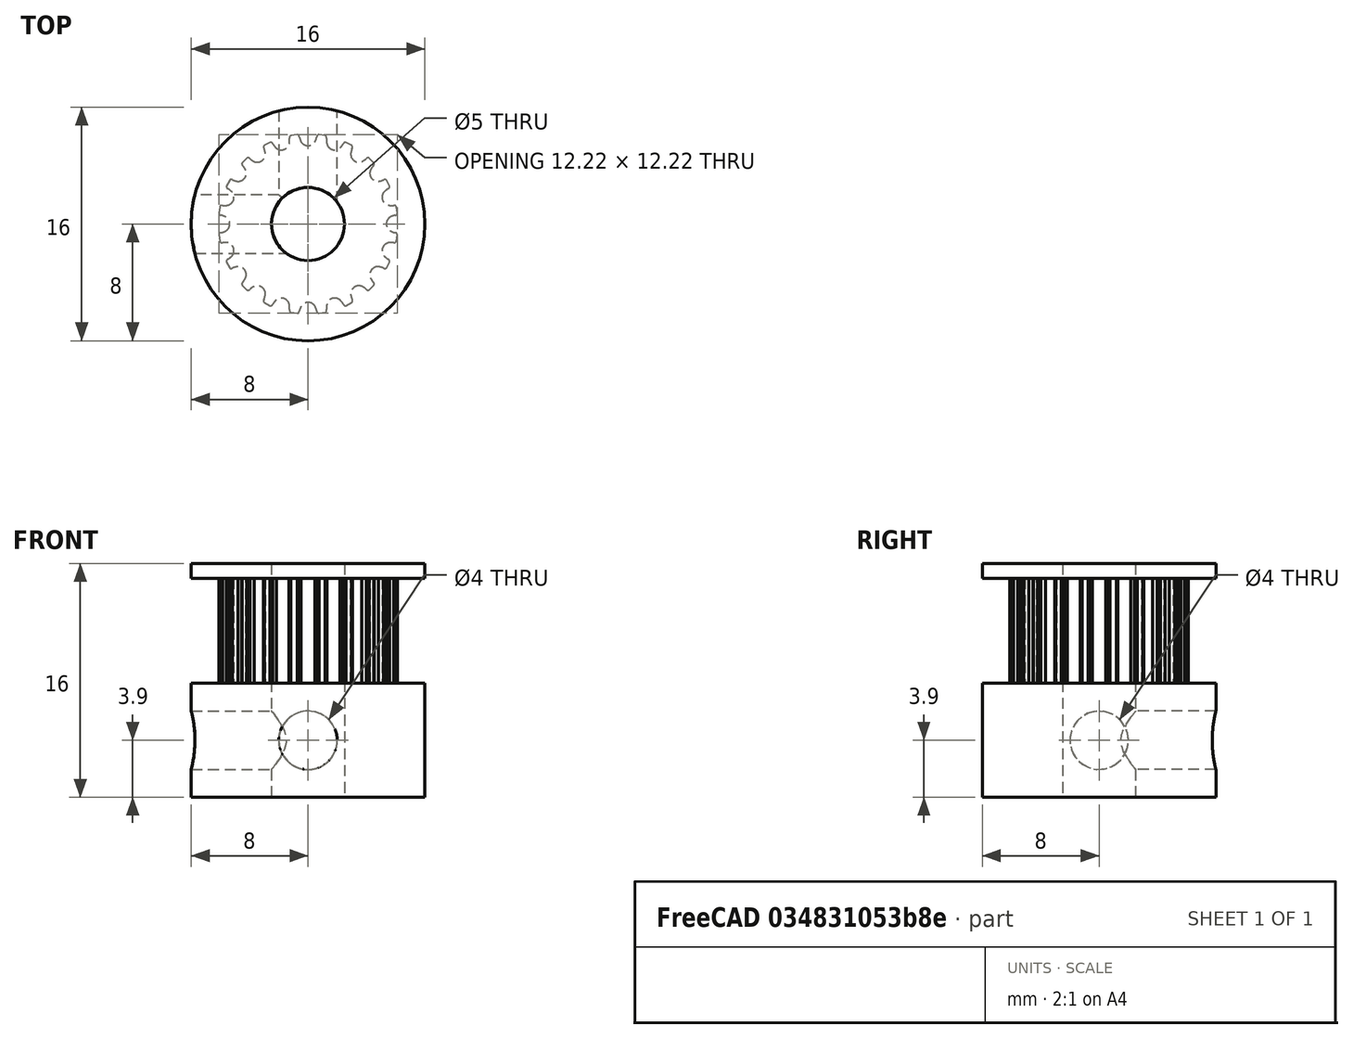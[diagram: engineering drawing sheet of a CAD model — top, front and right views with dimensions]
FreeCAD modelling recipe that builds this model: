
FCSTD DOCUMENT  (FreeCAD 0.21R33771 (Git))
Label: timing_pulley_gt2_20teeth_bore5
License: All rights reserved
LicenseURL: http://en.wikipedia.org/wiki/All_rights_reserved
objects: Sketcher::SketchObject×5, PartDesign::Pad×3, PartDesign::Pocket×2, PartDesign::Body×1
note: 16 computed .brp shape members not serialized (recipe doc carries the construction recipe); baked Part::Feature solids carry a one-line shape summary decoded from their .brp

FEATURE [Sketcher::SketchObject] SketchGear
  FullyConstrained = false
  MapMode = 5
  Support = -> [XY_Plane]
  sketch-geometry (121):
    g0: ArcOfCircle CenterX=5.9622 CenterY=-0.75 CenterZ=0 NormalX=0 NormalY=0 NormalZ=1 AngleXU=8.1e-15 Radius=0.15 StartAngle=0 EndAngle=1.5708
    g1: ArcOfCircle CenterX=6.30816 CenterY=0.82798 CenterZ=0 NormalX=0 NormalY=0 NormalZ=-1 AngleXU=-1.3331 Radius=1.46929 StartAngle=0 EndAngle=0.255762
    g2: ArcOfCircle CenterX=5.92156 CenterY=0 CenterZ=0 NormalX=0 NormalY=0 NormalZ=-1 AngleXU=-0.984764 Radius=0.559359 StartAngle=0 EndAngle=1.96953
    g3: ArcOfCircle CenterX=6.30816 CenterY=-0.82798 CenterZ=0 NormalX=0 NormalY=0 NormalZ=-1 AngleXU=1.07734 Radius=1.46929 StartAngle=0 EndAngle=0.255762
    g4: ArcOfCircle CenterX=5.9622 CenterY=0.75 CenterZ=0 NormalX=0 NormalY=0 NormalZ=1 AngleXU=-1.5708 Radius=0.15 StartAngle=0 EndAngle=1.5708
    g5: LineSegment StartX=6.1122 StartY=0.75 StartZ=0 EndX=6.04481 EndY=1.17548 EndZ=0
    g6: ArcOfCircle CenterX=5.90215 CenterY=1.12913 CenterZ=0 NormalX=0 NormalY=0 NormalZ=1 AngleXU=0.314159 Radius=0.15 StartAngle=0 EndAngle=1.5708
    g7: ArcOfCircle CenterX=5.74356 CenterY=2.73679 CenterZ=0 NormalX=0 NormalY=0 NormalZ=-1 AngleXU=-1.64726 Radius=1.46929 StartAngle=0 EndAngle=0.255762
    g8: ArcOfCircle CenterX=5.63174 CenterY=1.82986 CenterZ=0 NormalX=0 NormalY=0 NormalZ=-1 AngleXU=-1.29892 Radius=0.559359 StartAngle=0 EndAngle=1.96953
    g9: ArcOfCircle CenterX=6.25528 CenterY=1.16187 CenterZ=0 NormalX=0 NormalY=0 NormalZ=-1 AngleXU=0.763178 Radius=1.46929 StartAngle=0 EndAngle=0.255762
    g10: ArcOfCircle CenterX=5.43862 CenterY=2.55571 CenterZ=0 NormalX=0 NormalY=0 NormalZ=1 AngleXU=-1.25664 Radius=0.15 StartAngle=0 EndAngle=1.5708
    g11: LineSegment StartX=5.58128 StartY=2.60207 StartZ=0 EndX=5.38571 EndY=2.9859 EndZ=0
    g12: ArcOfCircle CenterX=5.26436 CenterY=2.89773 CenterZ=0 NormalX=0 NormalY=0 NormalZ=1 AngleXU=0.628319 Radius=0.15 StartAngle=0 EndAngle=1.5708
    g13: ArcOfCircle CenterX=4.61674 CenterY=4.3777 CenterZ=0 NormalX=0 NormalY=0 NormalZ=-1 AngleXU=-1.96142 Radius=1.46929 StartAngle=0 EndAngle=0.255762
    g14: ArcOfCircle CenterX=4.79064 CenterY=3.4806 CenterZ=0 NormalX=0 NormalY=0 NormalZ=-1 AngleXU=-1.61308 Radius=0.559359 StartAngle=0 EndAngle=1.96953
    g15: ArcOfCircle CenterX=5.59009 CenterY=3.038 CenterZ=0 NormalX=0 NormalY=0 NormalZ=-1 AngleXU=0.449019 Radius=1.46929 StartAngle=0 EndAngle=0.255762
    g16: ArcOfCircle CenterX=4.38268 CenterY=4.11125 CenterZ=0 NormalX=0 NormalY=0 NormalZ=1 AngleXU=-0.942478 Radius=0.15 StartAngle=0 EndAngle=1.5708
    g17: LineSegment StartX=4.50403 StartY=4.19942 StartZ=0 EndX=4.19942 EndY=4.50403 EndZ=0
    g18: ArcOfCircle CenterX=4.11125 CenterY=4.38268 CenterZ=0 NormalX=0 NormalY=0 NormalZ=1 AngleXU=0.942478 Radius=0.15 StartAngle=0 EndAngle=1.5708
    g19: ArcOfCircle CenterX=3.038 CenterY=5.59009 CenterZ=0 NormalX=0 NormalY=0 NormalZ=-1 AngleXU=-2.27558 Radius=1.46929 StartAngle=0 EndAngle=0.255762
    g20: ArcOfCircle CenterX=3.4806 CenterY=4.79064 CenterZ=0 NormalX=0 NormalY=0 NormalZ=-1 AngleXU=-1.92724 Radius=0.559359 StartAngle=0 EndAngle=1.96953
    g21: ArcOfCircle CenterX=4.3777 CenterY=4.61674 CenterZ=0 NormalX=0 NormalY=0 NormalZ=-1 AngleXU=0.13486 Radius=1.46929 StartAngle=0 EndAngle=0.255762
    g22: ArcOfCircle CenterX=2.89773 CenterY=5.26436 CenterZ=0 NormalX=0 NormalY=0 NormalZ=1 AngleXU=-0.628319 Radius=0.15 StartAngle=0 EndAngle=1.5708
    g23: LineSegment StartX=2.9859 StartY=5.38571 StartZ=0 EndX=2.60207 EndY=5.58128 EndZ=0
    g24: ArcOfCircle CenterX=2.55571 CenterY=5.43862 CenterZ=0 NormalX=0 NormalY=0 NormalZ=1 AngleXU=1.25664 Radius=0.15 StartAngle=0 EndAngle=1.5708
    g25: ArcOfCircle CenterX=1.16187 CenterY=6.25528 CenterZ=0 NormalX=0 NormalY=0 NormalZ=-1 AngleXU=-2.58974 Radius=1.46929 StartAngle=0 EndAngle=0.255762
    g26: ArcOfCircle CenterX=1.82986 CenterY=5.63174 CenterZ=0 NormalX=0 NormalY=0 NormalZ=-1 AngleXU=-2.2414 Radius=0.559359 StartAngle=0 EndAngle=1.96953
    g27: ArcOfCircle CenterX=2.73679 CenterY=5.74356 CenterZ=0 NormalX=0 NormalY=0 NormalZ=-1 AngleXU=-0.1793 Radius=1.46929 StartAngle=0 EndAngle=0.255762
    g28: ArcOfCircle CenterX=1.12913 CenterY=5.90215 CenterZ=0 NormalX=0 NormalY=0 NormalZ=1 AngleXU=-0.314159 Radius=0.15 StartAngle=0 EndAngle=1.5708
    g29: LineSegment StartX=1.17548 StartY=6.04481 StartZ=0 EndX=0.75 EndY=6.1122 EndZ=0
    g30: ArcOfCircle CenterX=0.75 CenterY=5.9622 CenterZ=0 NormalX=0 NormalY=0 NormalZ=1 AngleXU=1.5708 Radius=0.15 StartAngle=0 EndAngle=1.5708
    g31: ArcOfCircle CenterX=-0.82798 CenterY=6.30816 CenterZ=0 NormalX=0 NormalY=0 NormalZ=-1 AngleXU=-2.9039 Radius=1.46929 StartAngle=0 EndAngle=0.255762
    g32: ArcOfCircle CenterX=3e-16 CenterY=5.92156 CenterZ=0 NormalX=0 NormalY=0 NormalZ=-1 AngleXU=-2.55556 Radius=0.559359 StartAngle=0 EndAngle=1.96953
    g33: ArcOfCircle CenterX=0.82798 CenterY=6.30816 CenterZ=0 NormalX=0 NormalY=0 NormalZ=-1 AngleXU=-0.493459 Radius=1.46929 StartAngle=0 EndAngle=0.255762
    g34: ArcOfCircle CenterX=-0.75 CenterY=5.9622 CenterZ=0 NormalX=0 NormalY=0 NormalZ=1 AngleXU=5.9e-15 Radius=0.15 StartAngle=0 EndAngle=1.5708
    g35: LineSegment StartX=-0.75 StartY=6.1122 StartZ=0 EndX=-1.17548 EndY=6.04481 EndZ=0
    g36: ArcOfCircle CenterX=-1.12913 CenterY=5.90215 CenterZ=0 NormalX=0 NormalY=0 NormalZ=1 AngleXU=1.88496 Radius=0.15 StartAngle=0 EndAngle=1.5708
    g37: ArcOfCircle CenterX=-2.73679 CenterY=5.74356 CenterZ=0 NormalX=0 NormalY=0 NormalZ=-1 AngleXU=3.06513 Radius=1.46929 StartAngle=0 EndAngle=0.255762
    g38: ArcOfCircle CenterX=-1.82986 CenterY=5.63174 CenterZ=0 NormalX=0 NormalY=0 NormalZ=-1 AngleXU=-2.86972 Radius=0.559359 StartAngle=0 EndAngle=1.96953
    g39: ArcOfCircle CenterX=-1.16187 CenterY=6.25528 CenterZ=0 NormalX=0 NormalY=0 NormalZ=-1 AngleXU=-0.807618 Radius=1.46929 StartAngle=0 EndAngle=0.255762
    g40: ArcOfCircle CenterX=-2.55571 CenterY=5.43862 CenterZ=0 NormalX=0 NormalY=0 NormalZ=1 AngleXU=0.314159 Radius=0.15 StartAngle=0 EndAngle=1.5708
    g41: LineSegment StartX=-2.60207 StartY=5.58128 StartZ=0 EndX=-2.9859 EndY=5.38571 EndZ=0
    g42: ArcOfCircle CenterX=-2.89773 CenterY=5.26436 CenterZ=0 NormalX=0 NormalY=0 NormalZ=1 AngleXU=2.19911 Radius=0.15 StartAngle=0 EndAngle=1.5708
    g43: ArcOfCircle CenterX=-4.3777 CenterY=4.61674 CenterZ=0 NormalX=0 NormalY=0 NormalZ=-1 AngleXU=2.75097 Radius=1.46929 StartAngle=0 EndAngle=0.255762
    g44: ArcOfCircle CenterX=-3.4806 CenterY=4.79064 CenterZ=0 NormalX=0 NormalY=0 NormalZ=-1 AngleXU=3.09931 Radius=0.559359 StartAngle=0 EndAngle=1.96953
    g45: ArcOfCircle CenterX=-3.038 CenterY=5.59009 CenterZ=0 NormalX=0 NormalY=0 NormalZ=-1 AngleXU=-1.12178 Radius=1.46929 StartAngle=0 EndAngle=0.255762
    g46: ArcOfCircle CenterX=-4.11125 CenterY=4.38268 CenterZ=0 NormalX=0 NormalY=0 NormalZ=1 AngleXU=0.628319 Radius=0.15 StartAngle=0 EndAngle=1.5708
    g47: LineSegment StartX=-4.19942 StartY=4.50403 StartZ=0 EndX=-4.50403 EndY=4.19942 EndZ=0
    g48: ArcOfCircle CenterX=-4.38268 CenterY=4.11125 CenterZ=0 NormalX=0 NormalY=0 NormalZ=1 AngleXU=2.51327 Radius=0.15 StartAngle=0 EndAngle=1.5708
    g49: ArcOfCircle CenterX=-5.59009 CenterY=3.038 CenterZ=0 NormalX=0 NormalY=0 NormalZ=-1 AngleXU=2.43681 Radius=1.46929 StartAngle=0 EndAngle=0.255762
    g50: ArcOfCircle CenterX=-4.79064 CenterY=3.4806 CenterZ=0 NormalX=0 NormalY=0 NormalZ=-1 AngleXU=2.78515 Radius=0.559359 StartAngle=0 EndAngle=1.96953
    g51: ArcOfCircle CenterX=-4.61674 CenterY=4.3777 CenterZ=0 NormalX=0 NormalY=0 NormalZ=-1 AngleXU=-1.43594 Radius=1.46929 StartAngle=0 EndAngle=0.255762
    g52: ArcOfCircle CenterX=-5.26436 CenterY=2.89773 CenterZ=0 NormalX=0 NormalY=0 NormalZ=1 AngleXU=0.942478 Radius=0.15 StartAngle=0 EndAngle=1.5708
    g53: LineSegment StartX=-5.38571 StartY=2.9859 StartZ=0 EndX=-5.58128 EndY=2.60207 EndZ=0
    g54: ArcOfCircle CenterX=-5.43862 CenterY=2.55571 CenterZ=0 NormalX=0 NormalY=0 NormalZ=1 AngleXU=2.82743 Radius=0.15 StartAngle=0 EndAngle=1.5708
    g55: ArcOfCircle CenterX=-6.25528 CenterY=1.16187 CenterZ=0 NormalX=0 NormalY=0 NormalZ=-1 AngleXU=2.12265 Radius=1.46929 StartAngle=0 EndAngle=0.255762
    g56: ArcOfCircle CenterX=-5.63174 CenterY=1.82986 CenterZ=0 NormalX=0 NormalY=0 NormalZ=-1 AngleXU=2.47099 Radius=0.559359 StartAngle=0 EndAngle=1.96953
    g57: ArcOfCircle CenterX=-5.74356 CenterY=2.73679 CenterZ=0 NormalX=0 NormalY=0 NormalZ=-1 AngleXU=-1.7501 Radius=1.46929 StartAngle=0 EndAngle=0.255762
    g58: ArcOfCircle CenterX=-5.90215 CenterY=1.12913 CenterZ=0 NormalX=0 NormalY=0 NormalZ=1 AngleXU=1.25664 Radius=0.15 StartAngle=0 EndAngle=1.5708
    g59: LineSegment StartX=-6.04481 StartY=1.17548 StartZ=0 EndX=-6.1122 EndY=0.75 EndZ=0
    g60: ArcOfCircle CenterX=-5.9622 CenterY=0.75 CenterZ=0 NormalX=0 NormalY=0 NormalZ=1 AngleXU=-3.14159 Radius=0.15 StartAngle=0 EndAngle=1.5708
    g61: ArcOfCircle CenterX=-6.30816 CenterY=-0.82798 CenterZ=0 NormalX=0 NormalY=0 NormalZ=-1 AngleXU=1.80849 Radius=1.46929 StartAngle=0 EndAngle=0.255762
    g62: ArcOfCircle CenterX=-5.92156 CenterY=7e-16 CenterZ=0 NormalX=0 NormalY=0 NormalZ=-1 AngleXU=2.15683 Radius=0.559359 StartAngle=0 EndAngle=1.96953
    g63: ArcOfCircle CenterX=-6.30816 CenterY=0.82798 CenterZ=0 NormalX=0 NormalY=0 NormalZ=-1 AngleXU=-2.06426 Radius=1.46929 StartAngle=0 EndAngle=0.255762
    g64: ArcOfCircle CenterX=-5.9622 CenterY=-0.75 CenterZ=0 NormalX=0 NormalY=0 NormalZ=1 AngleXU=1.5708 Radius=0.15 StartAngle=0 EndAngle=1.5708
    g65: LineSegment StartX=-6.1122 StartY=-0.75 StartZ=0 EndX=-6.04481 EndY=-1.17548 EndZ=0
    g66: ArcOfCircle CenterX=-5.90215 CenterY=-1.12913 CenterZ=0 NormalX=0 NormalY=0 NormalZ=1 AngleXU=-2.82743 Radius=0.15 StartAngle=0 EndAngle=1.5708
    g67: ArcOfCircle CenterX=-5.74356 CenterY=-2.73679 CenterZ=0 NormalX=0 NormalY=0 NormalZ=-1 AngleXU=1.49433 Radius=1.46929 StartAngle=0 EndAngle=0.255762
    g68: ArcOfCircle CenterX=-5.63174 CenterY=-1.82986 CenterZ=0 NormalX=0 NormalY=0 NormalZ=-1 AngleXU=1.84267 Radius=0.559359 StartAngle=0 EndAngle=1.96953
    g69: ArcOfCircle CenterX=-6.25528 CenterY=-1.16187 CenterZ=0 NormalX=0 NormalY=0 NormalZ=-1 AngleXU=-2.37841 Radius=1.46929 StartAngle=0 EndAngle=0.255762
    g70: ArcOfCircle CenterX=-5.43862 CenterY=-2.55571 CenterZ=0 NormalX=0 NormalY=0 NormalZ=1 AngleXU=1.88496 Radius=0.15 StartAngle=0 EndAngle=1.5708
    g71: LineSegment StartX=-5.58128 StartY=-2.60207 StartZ=0 EndX=-5.38571 EndY=-2.9859 EndZ=0
    g72: ArcOfCircle CenterX=-5.26436 CenterY=-2.89773 CenterZ=0 NormalX=0 NormalY=0 NormalZ=1 AngleXU=-2.51327 Radius=0.15 StartAngle=0 EndAngle=1.5708
    g73: ArcOfCircle CenterX=-4.61674 CenterY=-4.3777 CenterZ=0 NormalX=0 NormalY=0 NormalZ=-1 AngleXU=1.18017 Radius=1.46929 StartAngle=0 EndAngle=0.255762
    g74: ArcOfCircle CenterX=-4.79064 CenterY=-3.4806 CenterZ=0 NormalX=0 NormalY=0 NormalZ=-1 AngleXU=1.52851 Radius=0.559359 StartAngle=0 EndAngle=1.96953
    g75: ArcOfCircle CenterX=-5.59009 CenterY=-3.038 CenterZ=0 NormalX=0 NormalY=0 NormalZ=-1 AngleXU=-2.69257 Radius=1.46929 StartAngle=0 EndAngle=0.255762
    g76: ArcOfCircle CenterX=-4.38268 CenterY=-4.11125 CenterZ=0 NormalX=0 NormalY=0 NormalZ=1 AngleXU=2.19911 Radius=0.15 StartAngle=0 EndAngle=1.5708
    g77: LineSegment StartX=-4.50403 StartY=-4.19942 StartZ=0 EndX=-4.19942 EndY=-4.50403 EndZ=0
    g78: ArcOfCircle CenterX=-4.11125 CenterY=-4.38268 CenterZ=0 NormalX=0 NormalY=0 NormalZ=1 AngleXU=-2.19911 Radius=0.15 StartAngle=0 EndAngle=1.5708
    g79: ArcOfCircle CenterX=-3.038 CenterY=-5.59009 CenterZ=0 NormalX=0 NormalY=0 NormalZ=-1 AngleXU=0.866016 Radius=1.46929 StartAngle=0 EndAngle=0.255762
    g80: ArcOfCircle CenterX=-3.4806 CenterY=-4.79064 CenterZ=0 NormalX=0 NormalY=0 NormalZ=-1 AngleXU=1.21435 Radius=0.559359 StartAngle=0 EndAngle=1.96953
    g81: ArcOfCircle CenterX=-4.3777 CenterY=-4.61674 CenterZ=0 NormalX=0 NormalY=0 NormalZ=-1 AngleXU=-3.00673 Radius=1.46929 StartAngle=0 EndAngle=0.255762
    g82: ArcOfCircle CenterX=-2.89773 CenterY=-5.26436 CenterZ=0 NormalX=0 NormalY=0 NormalZ=1 AngleXU=2.51327 Radius=0.15 StartAngle=0 EndAngle=1.5708
    g83: LineSegment StartX=-2.9859 StartY=-5.38571 StartZ=0 EndX=-2.60207 EndY=-5.58128 EndZ=0
    g84: ArcOfCircle CenterX=-2.55571 CenterY=-5.43862 CenterZ=0 NormalX=0 NormalY=0 NormalZ=1 AngleXU=-1.88496 Radius=0.15 StartAngle=0 EndAngle=1.5708
    g85: ArcOfCircle CenterX=-1.16187 CenterY=-6.25528 CenterZ=0 NormalX=0 NormalY=0 NormalZ=-1 AngleXU=0.551856 Radius=1.46929 StartAngle=0 EndAngle=0.255762
    g86: ArcOfCircle CenterX=-1.82986 CenterY=-5.63174 CenterZ=0 NormalX=0 NormalY=0 NormalZ=-1 AngleXU=0.900192 Radius=0.559359 StartAngle=0 EndAngle=1.96953
    g87: ArcOfCircle CenterX=-2.73679 CenterY=-5.74356 CenterZ=0 NormalX=0 NormalY=0 NormalZ=-1 AngleXU=2.96229 Radius=1.46929 StartAngle=0 EndAngle=0.255762
    g88: ArcOfCircle CenterX=-1.12913 CenterY=-5.90215 CenterZ=0 NormalX=0 NormalY=0 NormalZ=1 AngleXU=2.82743 Radius=0.15 StartAngle=0 EndAngle=1.5708
    g89: LineSegment StartX=-1.17548 StartY=-6.04481 StartZ=0 EndX=-0.75 EndY=-6.1122 EndZ=0
    g90: ArcOfCircle CenterX=-0.75 CenterY=-5.9622 CenterZ=0 NormalX=0 NormalY=0 NormalZ=1 AngleXU=-1.5708 Radius=0.15 StartAngle=0 EndAngle=1.5708
    g91: ArcOfCircle CenterX=0.82798 CenterY=-6.30816 CenterZ=0 NormalX=0 NormalY=0 NormalZ=-1 AngleXU=0.237697 Radius=1.46929 StartAngle=0 EndAngle=0.255762
    g92: ArcOfCircle CenterX=-1e-15 CenterY=-5.92156 CenterZ=0 NormalX=0 NormalY=0 NormalZ=-1 AngleXU=0.586033 Radius=0.559359 StartAngle=0 EndAngle=1.96953
    g93: ArcOfCircle CenterX=-0.82798 CenterY=-6.30816 CenterZ=0 NormalX=0 NormalY=0 NormalZ=-1 AngleXU=2.64813 Radius=1.46929 StartAngle=0 EndAngle=0.255762
    g94: ArcOfCircle CenterX=0.75 CenterY=-5.9622 CenterZ=0 NormalX=0 NormalY=0 NormalZ=1 AngleXU=-3.14159 Radius=0.15 StartAngle=0 EndAngle=1.5708
    g95: LineSegment StartX=0.75 StartY=-6.1122 StartZ=0 EndX=1.17548 EndY=-6.04481 EndZ=0
    g96: ArcOfCircle CenterX=1.12913 CenterY=-5.90215 CenterZ=0 NormalX=0 NormalY=0 NormalZ=1 AngleXU=-1.25664 Radius=0.15 StartAngle=0 EndAngle=1.5708
    g97: ArcOfCircle CenterX=2.73679 CenterY=-5.74356 CenterZ=0 NormalX=0 NormalY=0 NormalZ=-1 AngleXU=-0.0764622 Radius=1.46929 StartAngle=0 EndAngle=0.255762
    g98: ArcOfCircle CenterX=1.82986 CenterY=-5.63174 CenterZ=0 NormalX=0 NormalY=0 NormalZ=-1 AngleXU=0.271874 Radius=0.559359 StartAngle=0 EndAngle=1.96953
    g99: ArcOfCircle CenterX=1.16187 CenterY=-6.25528 CenterZ=0 NormalX=0 NormalY=0 NormalZ=-1 AngleXU=2.33397 Radius=1.46929 StartAngle=0 EndAngle=0.255762
    g100: ArcOfCircle CenterX=2.55571 CenterY=-5.43862 CenterZ=0 NormalX=0 NormalY=0 NormalZ=1 AngleXU=-2.82743 Radius=0.15 StartAngle=0 EndAngle=1.5708
    g101: LineSegment StartX=2.60207 StartY=-5.58128 StartZ=0 EndX=2.9859 EndY=-5.38571 EndZ=0
    g102: ArcOfCircle CenterX=2.89773 CenterY=-5.26436 CenterZ=0 NormalX=0 NormalY=0 NormalZ=1 AngleXU=-0.942478 Radius=0.15 StartAngle=0 EndAngle=1.5708
    g103: ArcOfCircle CenterX=4.3777 CenterY=-4.61674 CenterZ=0 NormalX=0 NormalY=0 NormalZ=-1 AngleXU=-0.390621 Radius=1.46929 StartAngle=0 EndAngle=0.255762
    g104: ArcOfCircle CenterX=3.4806 CenterY=-4.79064 CenterZ=0 NormalX=0 NormalY=0 NormalZ=-1 AngleXU=-0.0422858 Radius=0.559359 StartAngle=0 EndAngle=1.96953
    g105: ArcOfCircle CenterX=3.038 CenterY=-5.59009 CenterZ=0 NormalX=0 NormalY=0 NormalZ=-1 AngleXU=2.01982 Radius=1.46929 StartAngle=0 EndAngle=0.255762
    g106: ArcOfCircle CenterX=4.11125 CenterY=-4.38268 CenterZ=0 NormalX=0 NormalY=0 NormalZ=1 AngleXU=-2.51327 Radius=0.15 StartAngle=0 EndAngle=1.5708
    g107: LineSegment StartX=4.19942 StartY=-4.50403 StartZ=0 EndX=4.50403 EndY=-4.19942 EndZ=0
    g108: ArcOfCircle CenterX=4.38268 CenterY=-4.11125 CenterZ=0 NormalX=0 NormalY=0 NormalZ=1 AngleXU=-0.628319 Radius=0.15 StartAngle=0 EndAngle=1.5708
    g109: ArcOfCircle CenterX=5.59009 CenterY=-3.038 CenterZ=0 NormalX=0 NormalY=0 NormalZ=-1 AngleXU=-0.704781 Radius=1.46929 StartAngle=0 EndAngle=0.255762
    g110: ArcOfCircle CenterX=4.79064 CenterY=-3.4806 CenterZ=0 NormalX=0 NormalY=0 NormalZ=-1 AngleXU=-0.356445 Radius=0.559359 StartAngle=0 EndAngle=1.96953
    g111: ArcOfCircle CenterX=4.61674 CenterY=-4.3777 CenterZ=0 NormalX=0 NormalY=0 NormalZ=-1 AngleXU=1.70566 Radius=1.46929 StartAngle=0 EndAngle=0.255762
    g112: ArcOfCircle CenterX=5.26436 CenterY=-2.89773 CenterZ=0 NormalX=0 NormalY=0 NormalZ=1 AngleXU=-2.19911 Radius=0.15 StartAngle=0 EndAngle=1.5708
    g113: LineSegment StartX=5.38571 StartY=-2.9859 StartZ=0 EndX=5.58128 EndY=-2.60207 EndZ=0
    g114: ArcOfCircle CenterX=5.43862 CenterY=-2.55571 CenterZ=0 NormalX=0 NormalY=0 NormalZ=1 AngleXU=-0.314159 Radius=0.15 StartAngle=0 EndAngle=1.5708
    g115: ArcOfCircle CenterX=6.25528 CenterY=-1.16187 CenterZ=0 NormalX=0 NormalY=0 NormalZ=-1 AngleXU=-1.01894 Radius=1.46929 StartAngle=0 EndAngle=0.255762
    g116: ArcOfCircle CenterX=5.63174 CenterY=-1.82986 CenterZ=0 NormalX=0 NormalY=0 NormalZ=-1 AngleXU=-0.670604 Radius=0.559359 StartAngle=0 EndAngle=1.96953
    g117: ArcOfCircle CenterX=5.74356 CenterY=-2.73679 CenterZ=0 NormalX=0 NormalY=0 NormalZ=-1 AngleXU=1.3915 Radius=1.46929 StartAngle=0 EndAngle=0.255762
    g118: ArcOfCircle CenterX=5.90215 CenterY=-1.12913 CenterZ=0 NormalX=0 NormalY=0 NormalZ=1 AngleXU=-1.88496 Radius=0.15 StartAngle=0 EndAngle=1.5708
    g119: LineSegment StartX=6.04481 StartY=-1.17548 StartZ=0 EndX=6.1122 EndY=-0.75 EndZ=0
    g120: Circle CenterX=0 CenterY=0 CenterZ=0 NormalX=0 NormalY=0 NormalZ=1 AngleXU=0 Radius=2.5
FEATURE [PartDesign::Pad] Pad
  Direction = (0,0,1)
  Length = 7.2
  Length2 = 10
  Profile = -> SketchGear
  Refine = true
  Type = 0
FEATURE [Sketcher::SketchObject] SketchBase
  AttachmentOffset = pos=(0,0,-7.8) rot=(0,0,1;0rad)
  FullyConstrained = false
  MapMode = 5
  Placement = pos=(0,0,-7.8) rot=(0,0,1;0rad)
  Support = -> [XY_Plane]
  sketch-geometry (2):
    g0: Circle CenterX=0 CenterY=0 CenterZ=0 NormalX=0 NormalY=0 NormalZ=1 AngleXU=0 Radius=8
    g1: Circle CenterX=0 CenterY=0 CenterZ=0 NormalX=0 NormalY=0 NormalZ=1 AngleXU=0 Radius=2.5
FEATURE [PartDesign::Pad] PadBase
  BaseFeature = -> Pad
  Direction = (0,0,1)
  Length = 7.8
  Length2 = 10
  Profile = -> SketchBase
  Refine = true
  Type = 0
FEATURE [Sketcher::SketchObject] SketchTop
  AttachmentOffset = pos=(0,0,7.2) rot=(0,0,1;0rad)
  FullyConstrained = false
  MapMode = 5
  Placement = pos=(0,0,7.2) rot=(0,0,1;0rad)
  Support = -> [XY_Plane]
  sketch-geometry (2):
    g0: Circle CenterX=0 CenterY=0 CenterZ=0 NormalX=0 NormalY=0 NormalZ=1 AngleXU=0 Radius=8
    g1: Circle CenterX=0 CenterY=0 CenterZ=0 NormalX=0 NormalY=0 NormalZ=1 AngleXU=0 Radius=2.5
FEATURE [PartDesign::Pad] PadTop
  BaseFeature = -> PadBase
  Direction = (0,0,1)
  Length = 1
  Length2 = 10
  Profile = -> SketchTop
  Refine = true
  Type = 0
FEATURE [Sketcher::SketchObject] Sketch  label="sketch_mounting_hole1"
  FullyConstrained = true
  MapMode = 5
  Placement = pos=(0,0,0) rot=(0.57735,0.57735,0.57735;2.0944rad)
  Support = -> [YZ_Plane]
  sketch-geometry (1):
    g0: Circle CenterX=0 CenterY=-3.9 CenterZ=0 NormalX=0 NormalY=0 NormalZ=1 AngleXU=0 Radius=2
  constraints (3):
    c: PointOnObject(g0,g-2)
    c: Diameter(g0) = 4
    c: DistanceY(g0,g-1) = 3.9
FEATURE [PartDesign::Pocket] Pocket  label="pocket_mounting_hole1"
  BaseFeature = -> PadTop
  Direction = (-1,2e-16,-3e-16)
  Length = 5
  Length2 = 5
  Profile = -> Sketch
  ReferenceAxis = -> Sketch [N_Axis]
  Refine = true
  Type = 1
FEATURE [Sketcher::SketchObject] Sketch001  label="sketch_mounting_hole2"
  FullyConstrained = true
  MapMode = 5
  Placement = pos=(0,0,0) rot=(1,0,0;1.5708rad)
  Support = -> [XZ_Plane]
  sketch-geometry (1):
    g0: Circle CenterX=0 CenterY=-3.9 CenterZ=0 NormalX=0 NormalY=0 NormalZ=1 AngleXU=0 Radius=2
  constraints (3):
    c: PointOnObject(g0,g-2)
    c: Diameter(g0) = 4
    c: DistanceY(g0,g-1) = 3.9
FEATURE [PartDesign::Pocket] Pocket001  label="pocket_mounting_hole2"
  BaseFeature = -> Pocket
  Direction = (0,1,-2e-16)
  Length = 5
  Length2 = 5
  Profile = -> Sketch001
  ReferenceAxis = -> Sketch001 [N_Axis]
  Refine = true
  Type = 1
FEATURE [PartDesign::Body] Gear
  Group = -> [SketchGear,Pad,SketchBase,PadBase,SketchTop,PadTop,Sketch,Pocket,Sketch001,Pocket001]
  Origin = -> Origin
  Tip = -> Pocket001
